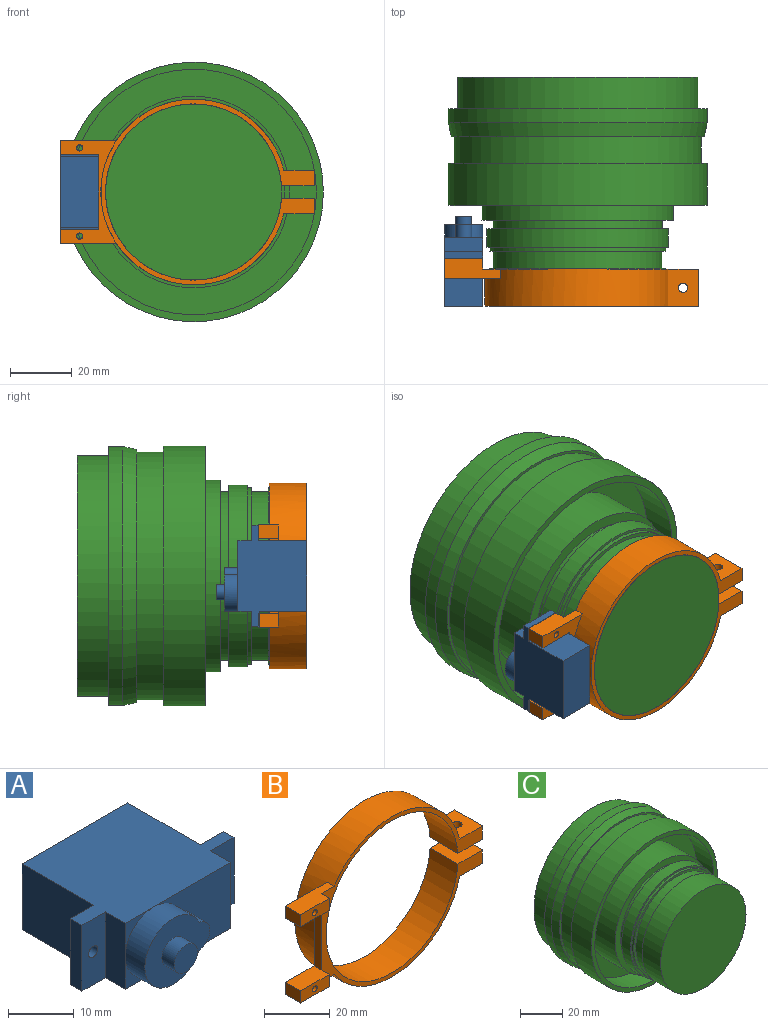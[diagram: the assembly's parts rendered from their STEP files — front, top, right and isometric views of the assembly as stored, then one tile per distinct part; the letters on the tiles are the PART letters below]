
ASSEMBLY  parts=3 mates=1
PART A: 23 faces, bbox 32.8x29.2x12.3 mm
  f0: plane 15.69x12.31mm, normal (1,0,0), area 193.1mm2, adj f6,f8,f10,f16
  f1: plane 15.44x12.31mm, normal (-1,0,0), area 190.1mm2, adj f6,f8,f10,f14
  f2: plane 16.65x12.31mm, normal (0,-1,0), area 138.3mm2, adj f3,f6,f7,f8,f12
  f3: cylinder r=6.16mm len=12.31mm, axis (0,1,0), area 141.5mm2, adj f2,f4,f5,f11,f12
  f4: plane 6.16x6.16mm, normal (0,-1,0), area 8.1mm2, adj f3,f8,f9
  f5: plane 6.16x6.16mm, normal (0,-1,0), area 8.1mm2, adj f3,f6,f9
  f6: plane 32.8x22.26mm, normal (0,0,-1), area 531.3mm2, adj f0,f1,f2,f5,f7,f9,f10,f13
  f7: plane 12.31x4.32mm, normal (1,0,0), area 53.2mm2, adj f2,f6,f8,f17
  f8: plane 32.8x22.26mm, normal (0,0,1), area 531.3mm2, adj f0,f1,f2,f4,f7,f9,f10,f13
  f9: plane 12.31x4.32mm, normal (-1,0,0), area 53.2mm2, adj f4,f5,f6,f8,f13
  f10: plane 22.8x12.31mm, normal (0,1,0), area 280.7mm2, adj f0,f1,f6,f8
  f11: plane 14.03x12.31mm, normal (0,-1,0), area 106.4mm2, adj f3,f12,f19
  f12: cylinder r=2.62mm len=5.21mm, axis (0,1,0), area 32.2mm2, adj f2,f3,f11
  f13: plane 12.31x5mm, normal (0,-1,0), area 58.4mm2, adj f6,f8,f9,f15,f22
  f14: plane 12.31x5mm, normal (0,1,0), area 58.4mm2, adj f1,f6,f8,f15,f22
  f15: plane 12.31x2.5mm, normal (-1,0,0), area 30.8mm2, adj f6,f8,f13,f14
  f16: plane 12.31x5mm, normal (0,1,0), area 58.4mm2, adj f0,f6,f8,f18,f21
  f17: plane 12.31x5mm, normal (0,-1,0), area 58.4mm2, adj f6,f7,f8,f18,f21
  f18: plane 12.31x2.25mm, normal (1,0,0), area 27.7mm2, adj f6,f8,f16,f17
  f19: cylinder r=2.5mm len=5mm, axis (0,1,0), area 42.1mm2, adj f11,f20
  f20: plane 5x5mm, normal (0,-1,0), area 19.6mm2, adj f19
  f21: cylinder r=1mm len=2.25mm, axis (0,-1,0), area 14.1mm2, adj f16,f17
  f22: cylinder r=1mm len=2.5mm, axis (0,-1,0), area 15.7mm2, adj f13,f14
PART B: 26 faces, bbox 82x15.5x60 mm
  f0: plane 69.69x60mm, normal (0,-1,0), area 443mm2, adj f3,f4,f6,f7,f8,f9,f10,f11
  f1: plane 6.5x4.5mm, normal (-1,0,0), area 29.2mm2, adj f2,f15,f21,f22
  f2: plane 33x17.95mm, normal (0,1,0), area 179.7mm2, adj f1,f9,f14,f15,f16,f18,f21,f23
  f3: plane 12x5mm, normal (1,0,0), area 60mm2, adj f0,f5,f6,f11
  f4: cylinder r=28.48mm len=56.95mm, axis (0,1,0), area 2098.9mm2, adj f0,f5,f10,f11
  f5: plane 69x60mm, normal (0,1,0), area 367.8mm2, adj f3,f4,f6,f7,f8,f9,f10,f11
  f6: plane 12x9.83mm, normal (0,0,-1), area 110.9mm2, adj f0,f3,f5,f9,f12
  f7: plane 12x5mm, normal (1,0,0), area 60mm2, adj f0,f5,f8,f10
  f8: plane 12x9.83mm, normal (0,0,1), area 110.9mm2, adj f0,f5,f7,f9,f13
  f9: cylinder r=30mm len=60mm, axis (0,1,0), area 1987.6mm2, adj f0,f2,f5,f6,f8,f14,f15
  f10: plane 12x10.6mm, normal (0,0,-1), area 120.1mm2, adj f0,f4,f5,f7,f13
  f11: plane 12x10.6mm, normal (0,0,1), area 120.1mm2, adj f0,f3,f4,f5,f12
  f12: cylinder r=1.5mm len=5mm, axis (0,0,-1), area 47.1mm2, adj f6,f11
  f13: cylinder r=1.5mm len=5mm, axis (0,0,-1), area 47.1mm2, adj f8,f10
  f14: plane 17.95x6.5mm, normal (0,0,1), area 96.9mm2, adj f0,f2,f9,f16,f17,f19
  f15: plane 17.95x6.5mm, normal (0,0,-1), area 96.9mm2, adj f0,f1,f2,f9,f20,f22
  f16: plane 6.5x4.5mm, normal (-1,0,0), area 29.2mm2, adj f2,f14,f18,f19
  f17: plane 4.5x3.5mm, normal (1,0,0), area 15.7mm2, adj f0,f14,f18,f19
  f18: plane 12.31x6.5mm, normal (0,0,-1), area 80mm2, adj f2,f16,f17,f19,f23
  f19: plane 12.31x4.5mm, normal (0,-1,0), area 52.3mm2, adj f14,f16,f17,f18,f25
  f20: plane 4.5x3.5mm, normal (1,0,0), area 15.7mm2, adj f0,f15,f21,f22
  f21: plane 12.31x6.5mm, normal (0,0,1), area 80mm2, adj f1,f2,f20,f22,f23
  f22: plane 12.31x4.5mm, normal (0,-1,0), area 52.3mm2, adj f1,f15,f20,f21,f24
  f23: plane 24x3mm, normal (-1,0,0), area 72mm2, adj f0,f2,f18,f21
  f24: cylinder r=1mm len=6.5mm, axis (0,1,0), area 40.8mm2, adj f2,f22
  f25: cylinder r=1mm len=6.5mm, axis (0,1,0), area 40.8mm2, adj f2,f19
PART C: 26 faces, bbox 83.9x74x83.9 mm
  f0: cylinder r=27.5mm len=55mm, axis (0,1,0), area 1752.1mm2, adj f2,f5
  f1: cylinder r=38.84mm len=77.68mm, axis (0,1,0), area 2474.6mm2, adj f2,f3
  f2: plane 77.68x77.68mm, normal (0,1,0), area 2363.4mm2, adj f0,f1
  f3: plane 83.75x83.75mm, normal (0,1,0), area 769.6mm2, adj f1,f4
  f4: cylinder r=41.88mm len=83.75mm, axis (0,1,0), area 1202.4mm2, adj f3,f7
  f5: plane 55x55mm, normal (0,1,0), area 2375.8mm2, adj f0
  f6: plane 81.85x81.85mm, normal (0,-1,0), area 235.2mm2, adj f7,f8
  f7: cone r=41.88mm half-angle=11.9deg, axis (0,1,0), area 1196.4mm2, adj f4,f6
  f8: cylinder r=40mm len=80mm, axis (0,1,0), area 2174mm2, adj f6,f11
  f9: cylinder r=41.95mm len=83.9mm, axis (0,1,0), area 3576.8mm2, adj f10,f11
  f10: plane 83.9x83.9mm, normal (0,-1,0), area 577.1mm2, adj f9,f12
  f11: plane 83.9x83.9mm, normal (0,1,0), area 502mm2, adj f8,f9
  f12: cylinder r=39.7mm len=79.4mm, axis (0,-1,0), area 2866.1mm2, adj f10,f13
  f13: plane 79.4x79.4mm, normal (0,-1,0), area 1932.4mm2, adj f12,f14
  f14: cylinder r=31mm len=62mm, axis (0,1,0), area 3172.9mm2, adj f13,f15
  f15: plane 62x62mm, normal (0,-1,0), area 678.4mm2, adj f14,f16
  f16: cylinder r=27.3mm len=54.59mm, axis (0,1,0), area 471.6mm2, adj f15,f19
  f17: cylinder r=29.38mm len=58.75mm, axis (0,1,0), area 1107.4mm2, adj f18,f19
  f18: plane 58.75x58.75mm, normal (0,-1,0), area 159.1mm2, adj f17,f20
  f19: plane 58.75x58.75mm, normal (0,1,0), area 370.2mm2, adj f16,f17
  f20: cylinder r=28.5mm len=57mm, axis (0,1,0), area 232.8mm2, adj f18,f21
  f21: plane 57x57mm, normal (0,-1,0), area 218.9mm2, adj f20,f22
  f22: cylinder r=27.25mm len=54.5mm, axis (0,1,0), area 941.7mm2, adj f21,f25
  f23: cylinder r=28.48mm len=56.95mm, axis (0,1,0), area 2191.7mm2, adj f24,f25
  f24: plane 56.95x56.95mm, normal (0,-1,0), area 2547.3mm2, adj f23
  f25: plane 56.95x56.95mm, normal (0,1,0), area 214.5mm2, adj f22,f23
PLACE A rot(axis=(0.71,0,0.71),180deg) t=(-71.87,-70.55,-46.49)mm
PLACE B rot(axis=(1,0,0),180deg) t=(-35.02,-70.36,-46.48)mm
PLACE C t=(-35.02,3.67,-46.48)mm
MATE fastened C.f0 <-> B.f4  axis (0,-1,0) through (-35.02,-70.36,-46.48)mm
